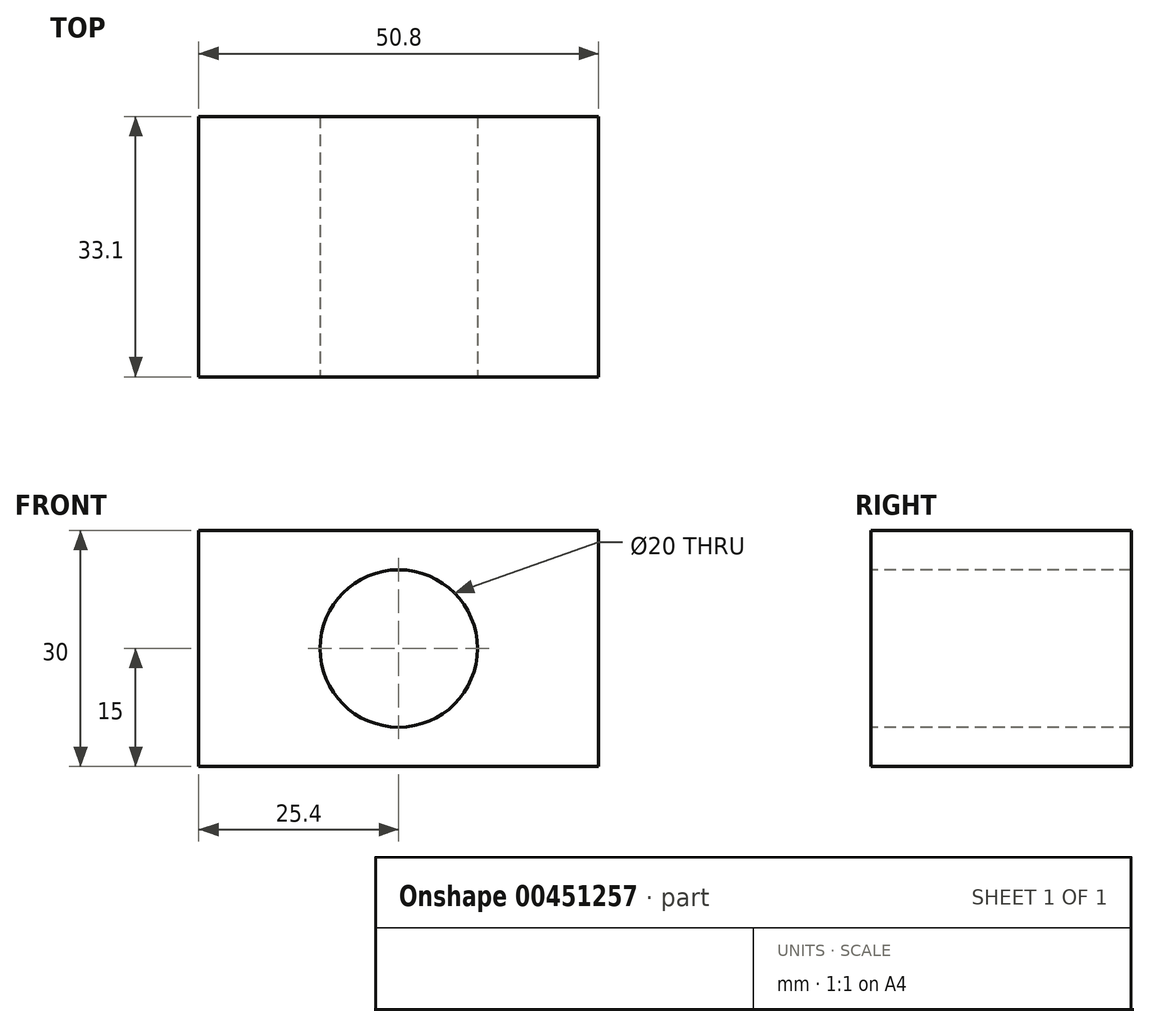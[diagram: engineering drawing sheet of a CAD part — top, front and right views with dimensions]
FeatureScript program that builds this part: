
annotation { "Feature Type Name" : "Feature", "Feature Type Description" : "" }
export const myFeature = defineFeature(function(context is Context, id is Id, definition is map)
    precondition{}
    {
        {
            var Q0;
            Q0=qCreatedBy(makeId("Front.planeOp"),FACE);
            var sketch = newSketch(context, id + "F0", { "sketchPlane" : qUnion([Q0])});
            skLineSegment(sketch, "E0.bottom", {"start": v(25.4, -15) * mm, "end": v(-25.4, -15) * mm});
            skLineSegment(sketch, "E0.top", {"start": v(25.4, 15) * mm, "end": v(-25.4, 15) * mm});
            skLineSegment(sketch, "E0.left", {"start": v(25.4, -15) * mm, "end": v(25.4, 15) * mm});
            skLineSegment(sketch, "E0.right", {"start": v(-25.4, -15) * mm, "end": v(-25.4, 15) * mm});
            skPoint(sketch, "E0.middle", {"position": v(0, 0) * mm});
            skCircle(sketch, "E1", {"center": v(0, 0) * mm, "radius": 10 * mm});
            skSolve(sketch);
        }
        {
            var Q0;
            Q0=makeQuery(id+"F0.imprint","IMPRINT",FACE,{"disambiguationData":[TD([[makeQuery(id+"F0.imprint","IMPRINT",EDGE,{"derivedFrom":sQuery(id+"F0.wireOp",EDGE,"E0.bottom")}),-1.0]])]});
            extrude(context, id + "F1", {"entities" : qUnion([Q0]), "oppositeDirection" : true, "depth" : 33.1 * mm});
        }
    });
